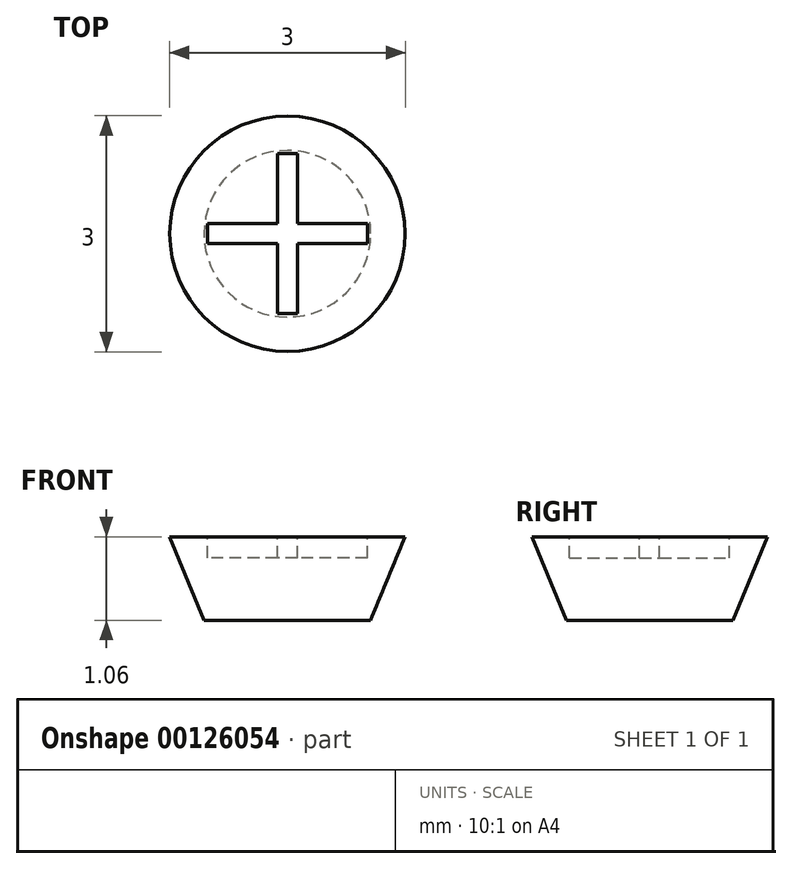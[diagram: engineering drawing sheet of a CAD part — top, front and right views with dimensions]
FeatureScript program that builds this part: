
annotation { "Feature Type Name" : "Feature", "Feature Type Description" : "" }
export const myFeature = defineFeature(function(context is Context, id is Id, definition is map)
    precondition{}
    {
        {
            var Q0;
            Q0=qCreatedBy(makeId("Front.planeOp"),FACE);
            var sketch = newSketch(context, id + "F0", { "sketchPlane" : qUnion([Q0])});
            skLineSegment(sketch, "E0", {"start": v(0, 0) * mm, "end": v(-1.06, 0) * mm});
            skLineSegment(sketch, "E1.MirrorCS", {"start": v(0, 1.06) * mm, "end": v(-1.5, 1.06) * mm});
            skLineSegment(sketch, "E2.MirrorCS", {"start": v(-1.5, 1.06) * mm, "end": v(-1.06, 0) * mm});
            skLineSegment(sketch, "E3", {"start": v(0, 1.06) * mm, "end": v(0, 0) * mm});
            skSolve(sketch);
        }
        {
            var Q0;
            Q0=makeQuery(id+"F0.imprint","IMPRINT",FACE,{"disambiguationData":[TD([[makeQuery(id+"F0.imprint","IMPRINT",EDGE,{"derivedFrom":sQuery(id+"F0.wireOp",EDGE,"E0")}),-1.0]])]});
            var Q1;
            Q1=sQuery(id+"F0.wireOp",EDGE,"E3");
            revolve(context, id + "F1", {"surfaceOperationType" : NewSurfaceOperationType.NEW, "entities" : qUnion([Q0]), "axis" : qUnion([Q1]), "revolveType" : RevolveType.FULL});
        }
        {
            var Q0;
            Q0=makeQuery(id+"F1.opRevolve","SWEPT_FACE",FACE,{"disambiguationData":[OSD([sQuery(id+"F0.wireOp",EDGE,"E1.MirrorCS")])]});
            var sketch = newSketch(context, id + "F2", { "sketchPlane" : qUnion([Q0])});
            skLineSegment(sketch, "E4.bottom", {"start": v(1.02, -0.13) * mm, "end": v(-1.02, -0.13) * mm});
            skLineSegment(sketch, "E4.top", {"start": v(1.02, 0.13) * mm, "end": v(-1.02, 0.13) * mm});
            skLineSegment(sketch, "E4.left", {"start": v(1.02, -0.13) * mm, "end": v(1.02, 0.13) * mm});
            skLineSegment(sketch, "E4.right", {"start": v(-1.02, -0.13) * mm, "end": v(-1.02, 0.13) * mm});
            skPoint(sketch, "E4.middle", {"position": v(0, 0) * mm});
            skLineSegment(sketch, "E5.bottom", {"start": v(0.13, -1.02) * mm, "end": v(-0.13, -1.02) * mm});
            skLineSegment(sketch, "E5.top", {"start": v(0.13, 1.02) * mm, "end": v(-0.13, 1.02) * mm});
            skLineSegment(sketch, "E5.left", {"start": v(0.13, -1.02) * mm, "end": v(0.13, 1.02) * mm});
            skLineSegment(sketch, "E5.right", {"start": v(-0.13, -1.02) * mm, "end": v(-0.13, 1.02) * mm});
            skSolve(sketch);
        }
        {
            var Q0;
            {var subQ5=sQuery(id+"F2.wireOp",EDGE,"E5.top");Q0=makeQuery(id+"F2.imprint","IMPRINT",FACE,{"disambiguationData":[TD([[makeQuery(id+"F2.imprint","IMPRINT",EDGE,{"derivedFrom":subQ5}),1.0]])]});}
            var Q1;
            {var subQ0=sQuery(id+"F2.wireOp",EDGE,"E5.left");var subQ1=sQuery(id+"F2.wireOp",EDGE,"E4.bottom");var subQ2=makeQuery(id+"F2.imprint","INTERSECT",VERTEX,{"derivedFrom":[subQ1,subQ0]});Q1=makeQuery(id+"F2.imprint","IMPRINT",FACE,{"disambiguationData":[TD([[makeQuery(id+"F2.imprint","IMPRINT",EDGE,{"disambiguationData":[TD([[subQ2,-1.0]])],"derivedFrom":subQ1}),-1.0]])]});}
            var Q2;
            {var subQ0=sQuery(id+"F2.wireOp",EDGE,"E4.right");Q2=makeQuery(id+"F2.imprint","IMPRINT",FACE,{"disambiguationData":[TD([[makeQuery(id+"F2.imprint","IMPRINT",EDGE,{"derivedFrom":subQ0}),-1.0]])]});}
            var Q3;
            {var subQ5=sQuery(id+"F2.wireOp",EDGE,"E5.bottom");Q3=makeQuery(id+"F2.imprint","IMPRINT",FACE,{"disambiguationData":[TD([[makeQuery(id+"F2.imprint","IMPRINT",EDGE,{"derivedFrom":subQ5}),-1.0]])]});}
            var Q4;
            {var subQ0=sQuery(id+"F2.wireOp",EDGE,"E4.left");Q4=makeQuery(id+"F2.imprint","IMPRINT",FACE,{"disambiguationData":[TD([[makeQuery(id+"F2.imprint","IMPRINT",EDGE,{"derivedFrom":subQ0}),1.0]])]});}
            extrude(context, id + "F3", {"entities" : qUnion([Q0, Q1, Q2, Q3, Q4]), "operationType" : NewBodyOperationType.REMOVE, "oppositeDirection" : true, "depth" : 0.26 * mm, "offsetDistance" : 25.4 * mm});
        }
    });
